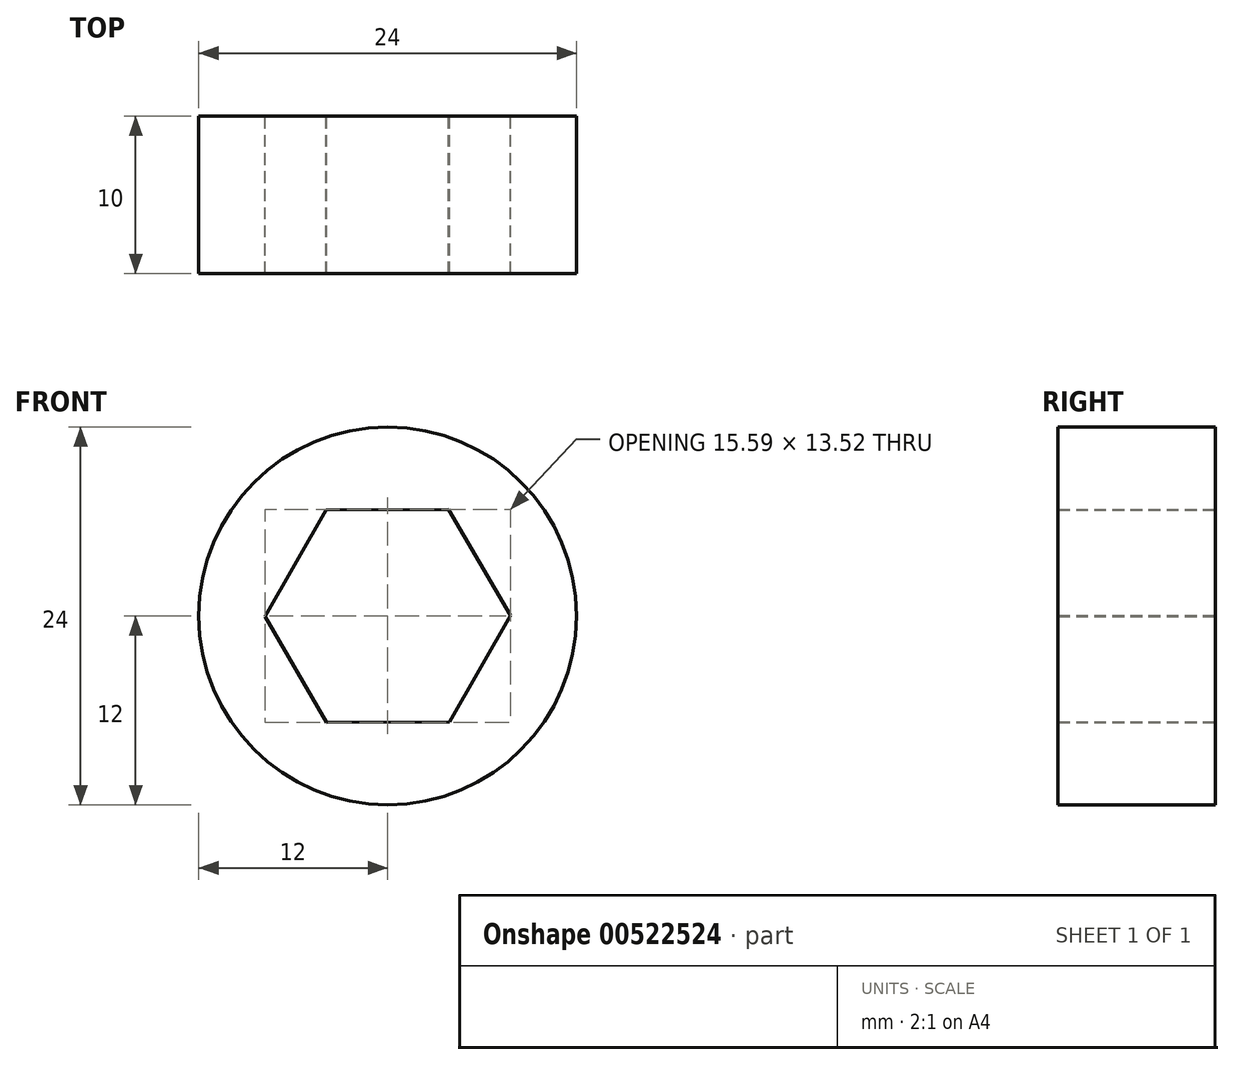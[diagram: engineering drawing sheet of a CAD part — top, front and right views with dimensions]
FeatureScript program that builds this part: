
annotation { "Feature Type Name" : "Feature", "Feature Type Description" : "" }
export const myFeature = defineFeature(function(context is Context, id is Id, definition is map)
    precondition{}
    {
        {
            assignVariable(context, id + "F0", {"name" : "thickness", "numberValue" : 10, "variableType" : VariableType.NUMBER});
        }
        {
            var Q0;
            Q0=qCreatedBy(makeId("Front.planeOp"),FACE);
            var sketch = newSketch(context, id + "F1", { "sketchPlane" : qUnion([Q0])});
            skCircle(sketch, "E0.cCircle", {"center": v(0, 0) * mm, "radius": 6.75 * mm, "construction": true});
            skLineSegment(sketch, "E0.0", {"start": v(7.8, 0.02) * mm, "end": v(3.92, -6.74) * mm});
            skLineSegment(sketch, "E0.1", {"start": v(3.92, -6.74) * mm, "end": v(-3.88, -6.76) * mm});
            skLineSegment(sketch, "E0.2", {"start": v(-3.88, -6.76) * mm, "end": v(-7.8, -0.02) * mm});
            skLineSegment(sketch, "E0.3", {"start": v(-7.8, -0.02) * mm, "end": v(-3.92, 6.74) * mm});
            skLineSegment(sketch, "E0.4", {"start": v(-3.92, 6.74) * mm, "end": v(3.88, 6.76) * mm});
            skLineSegment(sketch, "E0.5", {"start": v(3.88, 6.76) * mm, "end": v(7.8, 0.02) * mm});
            skPoint(sketch, "E0.0.midPoint", {"position": v(5.86, -3.36) * mm});
            skSolve(sketch);
        }
        {
            var Q0;
            Q0=qCreatedBy(makeId("Front.planeOp"),FACE);
            var sketch = newSketch(context, id + "F2", { "sketchPlane" : qUnion([Q0])});
            skCircle(sketch, "E1", {"center": v(0, 0) * mm, "radius": 12 * mm});
            skSolve(sketch);
        }
        {
            var Q0;
            Q0=makeQuery(id+"F2.imprint","IMPRINT",FACE,{"disambiguationData":[TD([[makeQuery(id+"F2.imprint","IMPRINT",EDGE,{"derivedFrom":sQuery(id+"F2.wireOp",EDGE,"E1")}),1.0]])]});
            var Q1;
            Q1=sQuery(id+"F2.wireOp",EDGE,"E1");
            extrude(context, id + "F3", {"entities" : qUnion([Q0]), "flatOperationType" : FlatOperationType.REMOVE, "surfaceEntities" : qUnion([Q1]), "depth" : (getVariable(context, 'thickness')) * mm, "offsetDistance" : 25 * mm, "domain" : OperationDomain.MODEL});
        }
        {
            var Q0;
            Q0=qSketchRegion(id+"F1",true);
            extrude(context, id + "F4", {"entities" : qUnion([Q0]), "operationType" : NewBodyOperationType.REMOVE, "depth" : (getVariable(context, 'thickness') * 2) * mm, "offsetDistance" : 25 * mm});
        }
    });
